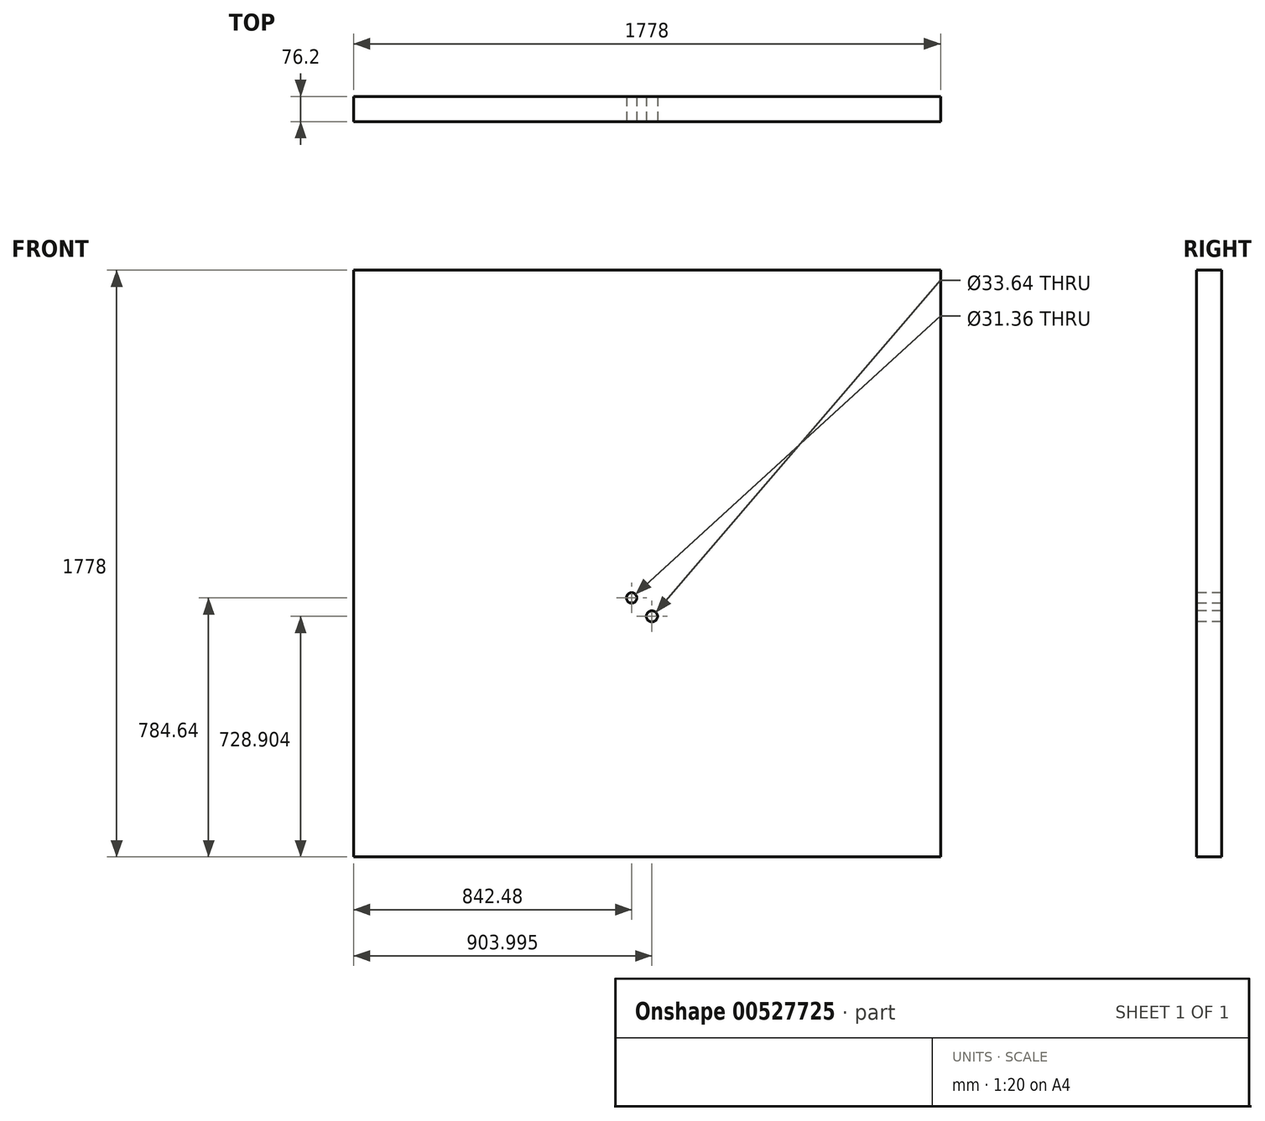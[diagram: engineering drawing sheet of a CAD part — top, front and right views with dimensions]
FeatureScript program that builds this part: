
annotation { "Feature Type Name" : "Feature", "Feature Type Description" : "" }
export const myFeature = defineFeature(function(context is Context, id is Id, definition is map)
    precondition{}
    {
        {
            var Q0;
            Q0=qCreatedBy(makeId("Front.planeOp"),FACE);
            var sketch = newSketch(context, id + "F0", { "sketchPlane" : qUnion([Q0])});
            skLineSegment(sketch, "E0.bottom", {"start": v(-886.33, 1026.9) * mm, "end": v(891.67, 1026.9) * mm});
            skLineSegment(sketch, "E0.top", {"start": v(-886.33, -751.1) * mm, "end": v(891.67, -751.1) * mm});
            skLineSegment(sketch, "E0.left", {"start": v(-886.33, 1026.9) * mm, "end": v(-886.33, -751.1) * mm});
            skLineSegment(sketch, "E0.right", {"start": v(891.67, 1026.9) * mm, "end": v(891.67, -751.1) * mm});
            skSolve(sketch);
        }
        {
            var Q0;
            Q0 = qSketchRegion(id + "F0", true);
            extrude(context, id + "F1", {"entities" : qUnion([Q0]), "depth" : 76.2 * mm, "offsetDistance" : 25.4 * mm});
        }
        {
            var Q0;
            Q0=makeQuery(id+"F1.opExtrude","CAP_FACE",FACE,{"disambiguationData":[OSD([sQuery(id+"F0.wireOp",EDGE,"E0.bottom"),sQuery(id+"F0.wireOp",EDGE,"E0.top"),sQuery(id+"F0.wireOp",EDGE,"E0.left"),sQuery(id+"F0.wireOp",EDGE,"E0.right")])],"isStart":false});
            var sketch = newSketch(context, id + "F2", { "sketchPlane" : qUnion([Q0])});
            skCircle(sketch, "E1", {"center": v(-43.85, 33.55) * mm, "radius": 15.68 * mm});
            skCircle(sketch, "E2", {"center": v(17.66, -22.19) * mm, "radius": 16.82 * mm});
            skSolve(sketch);
        }
        {
            var Q0;
            Q0 = qSketchRegion(id + "F2", true);
            extrude(context, id + "F3", {"entities" : qUnion([Q0]), "operationType" : NewBodyOperationType.REMOVE, "endBound" : BoundingType.UP_TO_NEXT, "oppositeDirection" : true, "depth" : 25.4 * mm, "offsetDistance" : 25.4 * mm});
        }
    });
